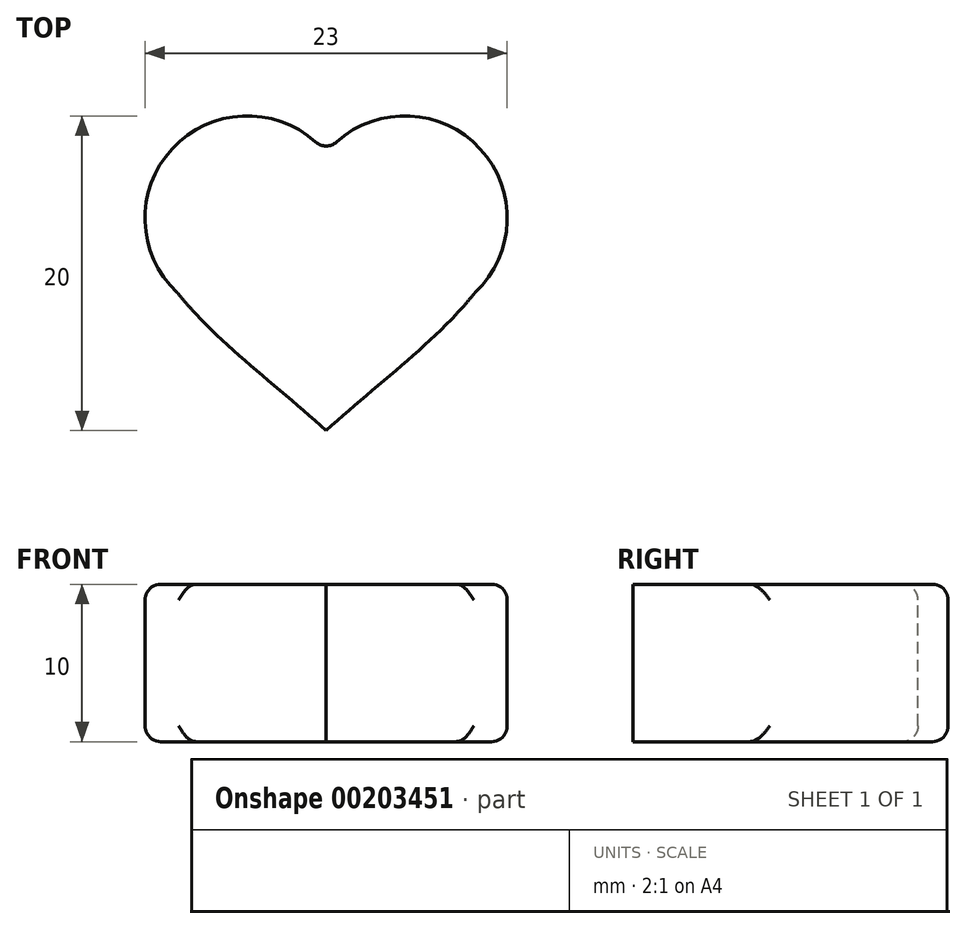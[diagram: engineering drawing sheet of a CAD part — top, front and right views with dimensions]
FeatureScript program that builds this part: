
annotation { "Feature Type Name" : "Feature", "Feature Type Description" : "" }
export const myFeature = defineFeature(function(context is Context, id is Id, definition is map)
    precondition{}
    {
        {
            var Q0;
            Q0=qCreatedBy(makeId("Top.planeOp"),FACE);
            var sketch = newSketch(context, id + "F0", { "sketchPlane" : qUnion([Q0])});
            skLineSegment(sketch, "E0.bottom", {"start": v(-11.5, 10) * mm, "end": v(11.5, 10) * mm, "construction": true});
            skLineSegment(sketch, "E0.top", {"start": v(-11.5, -10) * mm, "end": v(11.5, -10) * mm, "construction": true});
            skLineSegment(sketch, "E0.left", {"start": v(-11.5, 10) * mm, "end": v(-11.5, -10) * mm, "construction": true});
            skLineSegment(sketch, "E0.right", {"start": v(11.5, 10) * mm, "end": v(11.5, -10) * mm, "construction": true});
            skPoint(sketch, "E1", {"position": v(0, 10) * mm});
            skPoint(sketch, "E2", {"position": v(11.5, 0) * mm});
            skArc(sketch, "E3", {"start": v(0, 7.65) * mm, "mid": v(-9.47, 8.22) * mm, "end": v(-9.42, -1.27) * mm});
            skPoint(sketch, "E4", {"position": v(0, -10) * mm});
            skPoint(sketch, "E5", {"position": v(-9.42, -1.27) * mm});
            skPoint(sketch, "E6", {"position": v(9.42, -1.27) * mm});
            skFitSpline(sketch, "E7", {"points": [v(0, -10) * mm, v(-9.42, -1.27) * mm], "startDerivative": vector(-9.42, 8.73) * mm, "endDerivative": vector(-7.4, 9.34) * mm});
            skFitSpline(sketch, "E8.MirrorCS", {"points": [v(0, -10) * mm, v(9.42, -1.27) * mm], "startDerivative": vector(9.42, 8.73) * mm, "endDerivative": vector(7.4, 9.34) * mm});
            skArc(sketch, "E9", {"start": v(0, 7.65) * mm, "mid": v(9.47, 8.22) * mm, "end": v(9.42, -1.27) * mm});
            skPoint(sketch, "E10.end.orphan", {"position": v(-11.5, 0.66) * mm});
            skPoint(sketch, "E11.MirrorCS.end.orphan", {"position": v(11.5, 0.66) * mm});
            skSolve(sketch);
        }
        {
            var Q0;
            Q0=makeQuery(id+"F0.imprint","IMPRINT",FACE,{"disambiguationData":[TD([[makeQuery(id+"F0.imprint","IMPRINT",EDGE,{"derivedFrom":sQuery(id+"F0.wireOp",EDGE,"E3")}),1.0]])]});
            extrude(context, id + "F1", {"entities" : qUnion([Q0]), "depth" : 10 * mm});
        }
        {
            var Q0;
            Q0=makeQuery(id+"F1.opExtrude","SWEPT_FACE",FACE,{"disambiguationData":[OSD([sQuery(id+"F0.wireOp",EDGE,"E3")])]});
            var Q1;
            Q1=makeQuery(id+"F1.opExtrude","SWEPT_FACE",FACE,{"disambiguationData":[OSD([sQuery(id+"F0.wireOp",EDGE,"E9")])]});
            fillet(context, id + "F2", {"entities" : qUnion([Q0, Q1]), "radius" : 1 * mm, "tangentPropagation" : true, "allowEdgeOverflow" : false});
        }
    });
